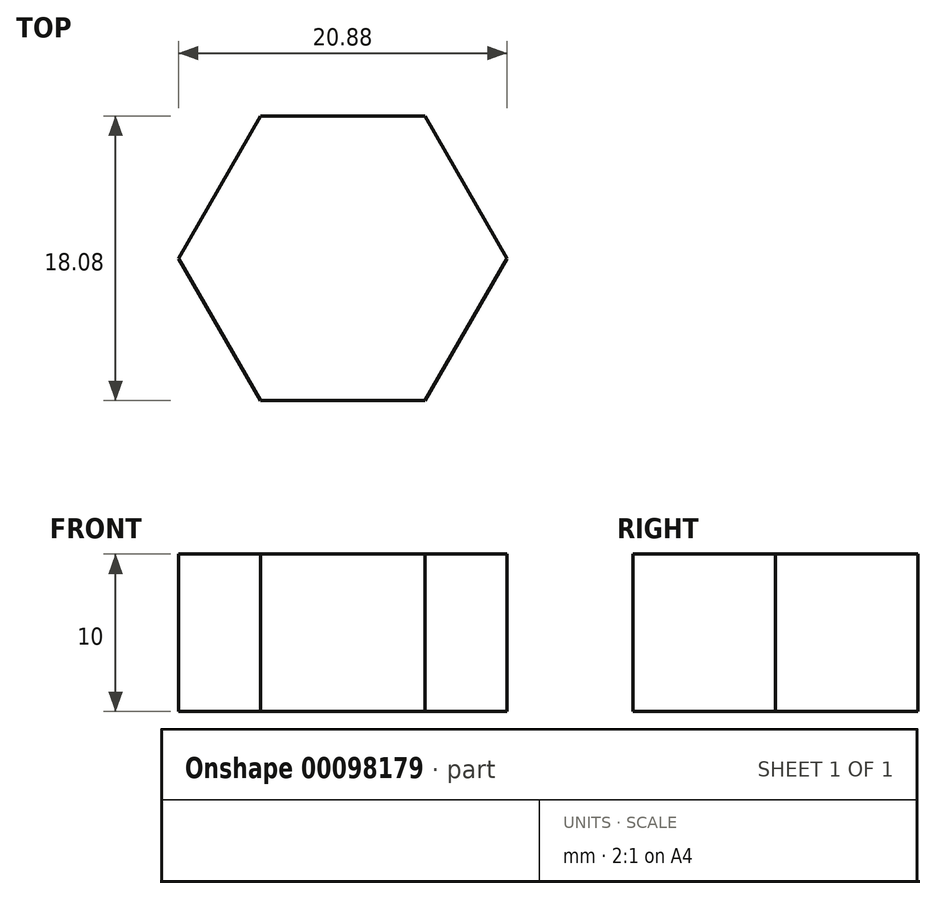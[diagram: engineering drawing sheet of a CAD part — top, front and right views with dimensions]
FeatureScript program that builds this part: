
annotation { "Feature Type Name" : "Feature", "Feature Type Description" : "" }
export const myFeature = defineFeature(function(context is Context, id is Id, definition is map)
    precondition{}
    {
        {
            var Q0;
            Q0=qCreatedBy(makeId("Top.planeOp"),FACE);
            var sketch = newSketch(context, id + "F0", { "sketchPlane" : qUnion([Q0])});
            skCircle(sketch, "E0", {"center": v(0, 0) * mm, "radius": 10.44 * mm});
            skCircle(sketch, "E1.cCircle", {"center": v(0, 0) * mm, "radius": 9.04 * mm, "construction": true});
            skLineSegment(sketch, "E1.0", {"start": v(5.22, 9.04) * mm, "end": v(10.44, 0) * mm});
            skLineSegment(sketch, "E1.1", {"start": v(10.44, 0) * mm, "end": v(5.22, -9.04) * mm});
            skLineSegment(sketch, "E1.2", {"start": v(5.22, -9.04) * mm, "end": v(-5.22, -9.04) * mm});
            skLineSegment(sketch, "E1.3", {"start": v(-5.22, -9.04) * mm, "end": v(-10.44, 0) * mm});
            skLineSegment(sketch, "E1.4", {"start": v(-10.44, 0) * mm, "end": v(-5.22, 9.04) * mm});
            skLineSegment(sketch, "E1.5", {"start": v(-5.22, 9.04) * mm, "end": v(5.22, 9.04) * mm});
            skPoint(sketch, "E1.0.midPoint", {"position": v(7.83, 4.52) * mm});
            skSolve(sketch);
        }
        {
            var Q0;
            Q0=makeQuery(id+"F0.imprint","IMPRINT",FACE,{"disambiguationData":[TD([[makeQuery(id+"F0.imprint","IMPRINT",EDGE,{"derivedFrom":sQuery(id+"F0.wireOp",EDGE,"E1.0")}),-1.0]])]});
            extrude(context, id + "F1", {"entities" : qUnion([Q0]), "depth" : 10 * mm, "offsetDistance" : 25 * mm});
        }
    });
